# Revit family: Hager-Univers-IP65-D200-H550-Cl.II-encl-NoHosted-CH-it
name_source: partatom
category: Electrical Equipment
units: mm (PartAtom-declared; Revit-internal decimal feet)

## family parameters
Always vertical = Yes
Cut with Voids When Loaded = No
Panel Configuration = Two Columns, Circuits Across
Part Type = Panelboard
Room Calculation Point = No
Round Connector Dimension = Use Diameter
Shared = No
Work Plane-Based = Yes

## types (1)
- A parete IP65 L300 A500 P200  - FL31S
    Default Elevation = 1219 mm
    EF000003 - Tipo di montaggio = EV000384 - A parete
    EF000007 - colore = EV000270 - grigio
    EF000008 - Larghezza = 300 mm  [stored 0.984252 ft]
    EF000040 - Altezza = 500 mm  [stored 1.64042 ft]
    EF000049 - profondità = 200 mm  [stored 0.656168 ft]
    EF000116 - numero RAL = 7035
    EF000118 - con piastra di montaggio = No
    EF000218 - profondità di incasso = 0 mm  [stored 0 ft]
    EF000266 - numero di file = 3
    EF000339 - tipo di copertura = EV004216 - porta
    EF000437 - numero di ingressi per conduttori = 0
    EF001088 - possibilità di applicazione = Yes
    EF001131 - profondità interna = 150 mm  [stored 0.492126 ft]
    EF001596 - Attacco Lampada = EV000139 - plastica
    EF001613 - Integrità del circuito = EV000494 - senza
    EF002950 - Numero moduli DIN = 12
    EF003532 - adatto per uso esterno = Yes
    EF004293 - resistenza agli urti = EV008784 - IK10
    EF004427 - numero di moduli = 36
    EF004464 - tipo di porta = EV002646 - singolo
    EF005474 - grado di protezione (IP) = EV006421 - IP65
    EF006244 - coperchio/porta trasparente = No
    EF006306 - con serratura = Yes
    EF007800 - adatto per parafulmine = Yes
    EF008873 - corrente nominale (In) = 630 A
    EF009170 - spessore materiale scatola = 1 mm  [stored 0.00328084 ft]
    EF009171 - spessore materiale porta/coperchio = 2 mm  [stored 0.00656168 ft]
    EF009212 - esecuzione coperchio = EV000116 - chiuso
    EF009554 - numero delle aperture per la piastra della flangia = 0
    EF015940 - Coprire con rilascio di sovrapressione = No
    HG000002 - Con porta = Yes
    HG000003 - Gamma = Univers
    HG000004 - Codice produttore = FL31S
    HG000006 - Ad incasso = No
    HG000009 - Porta doppia a battente = No
    HG000010 - Porte asimmetriche = No
    HG000023 - Custodia a doppia sezione = No
    HG000024 - Altezza della sezione inferiore = 600 mm
    HG000026 - A pavimento = No
    HG000027 - Altezza dello zoccolo = 0 mm  [stored 0 ft]
    Manufacturer = Hager
    Type Comments = Univers

note: [stored X ft] marks values corroborated as IEEE doubles in the binary element streams (Revit-internal decimal feet)

## geometry (parser evidence)
native form markers: Blend x4, Sweep x5
no freeform markers — native parametric forms only
